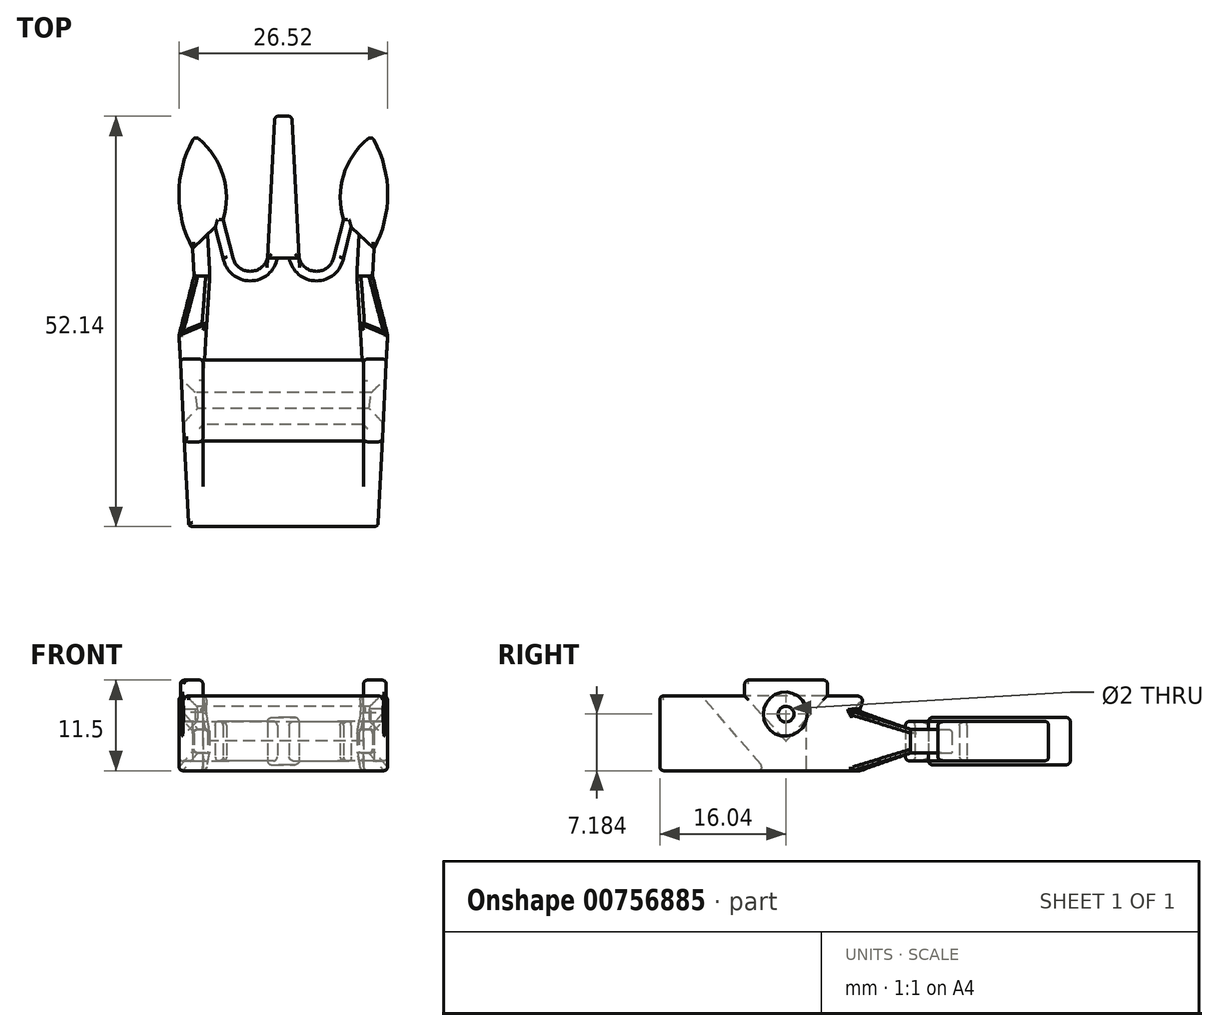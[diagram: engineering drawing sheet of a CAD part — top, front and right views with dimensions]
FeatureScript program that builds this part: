
annotation { "Feature Type Name" : "Feature", "Feature Type Description" : "" }
export const myFeature = defineFeature(function(context is Context, id is Id, definition is map)
    precondition{}
    {
        {
            var Q0;
            Q0=qCreatedBy(makeId("Top.planeOp"),FACE);
            var sketch = newSketch(context, id + "F0", { "sketchPlane" : qUnion([Q0])});
            skLineSegment(sketch, "E0", {"start": v(0, 0) * mm, "end": v(0, 18) * mm});
            skLineSegment(sketch, "E1", {"start": v(0, 0) * mm, "end": v(2, 0) * mm});
            skLineSegment(sketch, "E2", {"start": v(2, 0) * mm, "end": v(1.1, 18) * mm});
            skLineSegment(sketch, "E3", {"start": v(1.1, 18) * mm, "end": v(0, 18) * mm});
            skLineSegment(sketch, "E4", {"start": v(0, -15.6) * mm, "end": v(10.2, -15.6) * mm, "construction": true});
            skLineSegment(sketch, "E5", {"start": v(10.2, -15.6) * mm, "end": v(9.34, -2.3) * mm});
            skPoint(sketch, "E6", {"position": v(11.23, 15.5) * mm});
            skArc(sketch, "E7", {"start": v(11.53, 1.18) * mm, "mid": v(13.26, 8.38) * mm, "end": v(11.23, 15.5) * mm});
            skArc(sketch, "E8", {"start": v(11.23, 15.5) * mm, "mid": v(7.74, 10.76) * mm, "end": v(7.64, 4.86) * mm});
            skLineSegment(sketch, "E9", {"start": v(11.53, 1.18) * mm, "end": v(7.64, 4.86) * mm});
            skLineSegment(sketch, "E10", {"start": v(7.64, 4.86) * mm, "end": v(6.4, 0) * mm});
            skArc(sketch, "E11", {"start": v(2, 0) * mm, "mid": v(4.2, -1.7) * mm, "end": v(6.4, 0) * mm});
            skLineSegment(sketch, "E12", {"start": v(6.4, 0) * mm, "end": v(7.64, 0) * mm});
            skArc(sketch, "E13", {"start": v(0.76, 0) * mm, "mid": v(4.2, -2.92) * mm, "end": v(7.64, 0) * mm});
            skLineSegment(sketch, "E14", {"start": v(7.64, 0) * mm, "end": v(8.64, 3.92) * mm});
            skLineSegment(sketch, "E15", {"start": v(11.34, -2.3) * mm, "end": v(11.8, -9.27) * mm});
            skLineSegment(sketch, "E16", {"start": v(10.2, -15.6) * mm, "end": v(12.96, -15.6) * mm});
            skLineSegment(sketch, "E17", {"start": v(12.96, -15.6) * mm, "end": v(13.25, -9.87) * mm});
            skLineSegment(sketch, "E18", {"start": v(13.25, -9.87) * mm, "end": v(11.8, -9.27) * mm});
            skLineSegment(sketch, "E19", {"start": v(13.25, -9.87) * mm, "end": v(9.73, -8.42) * mm});
            skLineSegment(sketch, "E20", {"start": v(12.96, -15.6) * mm, "end": v(12.03, -34.14) * mm});
            skLineSegment(sketch, "E21", {"start": v(12.03, -34.14) * mm, "end": v(0, -34.14) * mm});
            skLineSegment(sketch, "E22", {"start": v(0, -34.14) * mm, "end": v(0, -28.82) * mm});
            skLineSegment(sketch, "E23", {"start": v(0, -28.82) * mm, "end": v(10.2, -28.82) * mm});
            skLineSegment(sketch, "E24", {"start": v(10.2, -15.6) * mm, "end": v(10.2, -28.82) * mm});
            skLineSegment(sketch, "E25", {"start": v(10.2, -20.6) * mm, "end": v(0, -20.6) * mm, "construction": true});
            skLineSegment(sketch, "E26", {"start": v(0, -20.6) * mm, "end": v(0, -15.6) * mm, "construction": true});
            skLineSegment(sketch, "E27", {"start": v(10.2, -20.6) * mm, "end": v(12.71, -20.6) * mm});
            skLineSegment(sketch, "E28", {"start": v(9.34, -2.3) * mm, "end": v(11.34, -2.3) * mm});
            skLineSegment(sketch, "E29", {"start": v(11.34, -2.3) * mm, "end": v(11.53, 1.18) * mm});
            skLineSegment(sketch, "E30", {"start": v(9.34, -2.3) * mm, "end": v(9.62, 2.99) * mm});
            skSolve(sketch);
        }
        {
            var Q0;
            {var subQ3=sQuery(id+"F0.wireOp",EDGE,"E0");Q0=makeQuery(id+"F0.imprint","IMPRINT",FACE,{"disambiguationData":[TD([[makeQuery(id+"F0.imprint","IMPRINT",EDGE,{"derivedFrom":subQ3}),-1.0]])]});}
            extrude(context, id + "F1", {"entities" : qUnion([Q0]), "depth" : 6 * mm, "offsetDistance" : 25 * mm, "symmetric" : true});
        }
        {
            var Q0;
            {var subQ0=sQuery(id+"F0.wireOp",EDGE,"E11");Q0=makeQuery(id+"F0.imprint","IMPRINT",FACE,{"disambiguationData":[TD([[makeQuery(id+"F0.imprint","IMPRINT",EDGE,{"derivedFrom":subQ0}),-1.0]])]});}
            var Q1;
            {var subQ0=sQuery(id+"F0.wireOp",EDGE,"E10");Q1=makeQuery(id+"F0.imprint","IMPRINT",FACE,{"disambiguationData":[TD([[makeQuery(id+"F0.imprint","IMPRINT",EDGE,{"derivedFrom":subQ0}),1.0]])]});}
            var Q2;
            {var subQ3=sQuery(id+"F0.wireOp",EDGE,"E7");Q2=makeQuery(id+"F0.imprint","IMPRINT",FACE,{"disambiguationData":[TD([[makeQuery(id+"F0.imprint","IMPRINT",EDGE,{"derivedFrom":subQ3}),1.0]])]});}
            extrude(context, id + "F2", {"entities" : qUnion([Q0, Q1, Q2]), "operationType" : NewBodyOperationType.ADD, "depth" : 5 * mm, "offsetDistance" : 25 * mm, "symmetric" : true});
        }
        {
            var Q0;
            {var subQ3=sQuery(id+"F0.wireOp",EDGE,"E28");Q0=makeQuery(id+"F0.imprint","IMPRINT",FACE,{"disambiguationData":[TD([[makeQuery(id+"F0.imprint","IMPRINT",EDGE,{"derivedFrom":subQ3}),1.0]])]});}
            extrude(context, id + "F3", {"entities" : qUnion([Q0]), "operationType" : NewBodyOperationType.ADD, "depth" : 3 * mm, "offsetDistance" : 25 * mm, "symmetric" : true});
        }
        {
            var Q0;
            {var subQ4=sQuery(id+"F0.wireOp",EDGE,"E16");Q0=makeQuery(id+"F0.imprint","IMPRINT",FACE,{"disambiguationData":[TD([[makeQuery(id+"F0.imprint","IMPRINT",EDGE,{"derivedFrom":subQ4}),1.0]])]});}
            var Q1;
            {var subQ0=sQuery(id+"F0.wireOp",EDGE,"E16");Q1=makeQuery(id+"F0.imprint","IMPRINT",FACE,{"disambiguationData":[TD([[makeQuery(id+"F0.imprint","IMPRINT",EDGE,{"derivedFrom":subQ0}),-1.0]])]});}
            var Q2;
            {var subQ0=sQuery(id+"F0.wireOp",EDGE,"jtnNCOtV-VjFS-6lRW-7qlV-mgHXxbnkHb78");Q2=makeQuery(id+"F0.imprint","IMPRINT",FACE,{"disambiguationData":[TD([[makeQuery(id+"F0.imprint","IMPRINT",EDGE,{"derivedFrom":subQ0}),-1.0]])]});}
            extrude(context, id + "F4", {"entities" : qUnion([Q0, Q1, Q2]), "depth" : 7.5 * mm, "offsetDistance" : 25 * mm, "symmetric" : true});
        }
        {
            var Q0;
            Q0=makeQuery(id+"F3.opExtrude","SWEPT_FACE",FACE,{"disambiguationData":[OSD([sQuery(id+"F0.wireOp",EDGE,"E28")])]});
            var Q1;
            Q1=makeQuery(id+"F4.opExtrude","SWEPT_FACE",FACE,{"disambiguationData":[OSD([sQuery(id+"F0.wireOp",EDGE,"E19")])]});
            loft(context, id + "F5", {"sheetProfilesArray" : [{ "sheetProfileEntities" : qUnion([Q0]) }, { "sheetProfileEntities" : qUnion([Q1]) }]});
        }
        {
            var Q0;
            {var subQ0=sQuery(id+"F0.wireOp",EDGE,"E21");Q0=makeQuery(id+"F0.imprint","IMPRINT",FACE,{"disambiguationData":[TD([[makeQuery(id+"F0.imprint","IMPRINT",EDGE,{"derivedFrom":subQ0}),-1.0]])]});}
            extrude(context, id + "F6", {"entities" : qUnion([Q0]), "operationType" : NewBodyOperationType.ADD, "depth" : 7.5 * mm, "offsetDistance" : 25 * mm, "symmetric" : true});
        }
        {
            var Q0;
            Q0=makeQuery(id+"F5.opLoft","SWEPT_BODY",BODY,{"disambiguationData":[OSD([sQuery(id+"F0.wireOp",EDGE,"E19"),sQuery(id+"F0.wireOp",EDGE,"E28")])]});
            var Q1;
            Q1=makeQuery(id+"F4.opExtrude","SWEPT_BODY",BODY,{"disambiguationData":[OSD([sQuery(id+"F0.wireOp",EDGE,"E5"),sQuery(id+"F0.wireOp",EDGE,"E17"),sQuery(id+"F0.wireOp",EDGE,"E19"),sQuery(id+"F0.wireOp",EDGE,"E20"),sQuery(id+"F0.wireOp",EDGE,"E24"),sQuery(id+"F0.wireOp",EDGE,"jtnNCOtV-VjFS-6lRW-7qlV-mgHXxbnkHb78"),sQuery(id+"F0.wireOp",EDGE,"VnQkR1Gs-op7I-iPq7-15UO-Wn8J0Wl9CDE5"),sQuery(id+"F0.wireOp",EDGE,"p3SSW1IA-Imiw-whqf-gpxS-0o3krwaSba9o"),sQuery(id+"F0.wireOp",EDGE,"E27")])]});
            var Q2;
            Q2=makeQuery(id+"F1.opExtrude","SWEPT_BODY",BODY,{"disambiguationData":[OSD([sQuery(id+"F0.wireOp",EDGE,"E0"),sQuery(id+"F0.wireOp",EDGE,"E1"),sQuery(id+"F0.wireOp",EDGE,"E2"),sQuery(id+"F0.wireOp",EDGE,"E3")])]});
            booleanBodies(context, id + "F7", {"operationType" : BooleanOperationType.UNION, "tools" : qUnion([Q0, Q1, Q2])});
        }
        {
            var Q0;
            {var subQ0=sQuery(id+"F0.wireOp",EDGE,"E27");var subQ1=sQuery(id+"F0.wireOp",EDGE,"E24");var subQ2=sQuery(id+"F0.wireOp",EDGE,"E20");Q0=makeQuery(id+"F6.boolean.opBoolean","MERGE",FACE,{"derivedFrom":[makeQuery(id+"F4.opExtrude","CAP_FACE",FACE,{"disambiguationData":[OSD([sQuery(id+"F0.wireOp",EDGE,"E5"),sQuery(id+"F0.wireOp",EDGE,"E17"),sQuery(id+"F0.wireOp",EDGE,"E19"),subQ2,subQ1,sQuery(id+"F0.wireOp",EDGE,"jtnNCOtV-VjFS-6lRW-7qlV-mgHXxbnkHb78"),sQuery(id+"F0.wireOp",EDGE,"VnQkR1Gs-op7I-iPq7-15UO-Wn8J0Wl9CDE5"),sQuery(id+"F0.wireOp",EDGE,"p3SSW1IA-Imiw-whqf-gpxS-0o3krwaSba9o"),subQ0])],"isStart":false}),makeQuery(id+"F6.opExtrude","CAP_FACE",FACE,{"disambiguationData":[OSD([subQ2,sQuery(id+"F0.wireOp",EDGE,"E21"),sQuery(id+"F0.wireOp",EDGE,"E22"),sQuery(id+"F0.wireOp",EDGE,"E23"),subQ1,subQ0])],"isStart":false})]});}
            extrude(context, id + "F8", {"entities" : qUnion([Q0]), "operationType" : NewBodyOperationType.ADD, "depth" : 2 * mm, "offsetDistance" : 25 * mm});
        }
        {
            var Q0;
            {var subQ0=sQuery(id+"F0.wireOp",EDGE,"E24");Q0=makeQuery(id+"F6.boolean.opBoolean","MERGE",FACE,{"derivedFrom":[makeQuery(id+"F4.opExtrude","SWEPT_FACE",FACE,{"disambiguationData":[OSD([subQ0])]}),makeQuery(id+"F6.opExtrude","SWEPT_FACE",FACE,{"disambiguationData":[OSD([subQ0])]})]});}
            var sketch = newSketch(context, id + "F9", { "sketchPlane" : qUnion([Q0])});
            skLineSegment(sketch, "E31", {"start": v(28.82, -3.75) * mm, "end": v(20.6, -3.75) * mm});
            skLineSegment(sketch, "E32", {"start": v(20.6, -3.75) * mm, "end": v(28.82, 5.75) * mm});
            skLineSegment(sketch, "E33", {"start": v(20.6, -3.75) * mm, "end": v(20.6, 0) * mm, "construction": true});
            skLineSegment(sketch, "E34", {"start": v(28.82, -3.75) * mm, "end": v(28.82, 5.75) * mm});
            skSolve(sketch);
        }
        {
            var Q0;
            Q0=makeQuery(id+"F9.imprint","IMPRINT",FACE,{"disambiguationData":[TD([[makeQuery(id+"F9.imprint","IMPRINT",EDGE,{"derivedFrom":sQuery(id+"F9.wireOp",EDGE,"E31")}),1.0]])]});
            var Q1;
            Q1=makeQuery(id+"F6.opExtrude","SWEPT_FACE",FACE,{"disambiguationData":[OSD([sQuery(id+"F0.wireOp",EDGE,"E22")])]});
            extrude(context, id + "F10", {"entities" : qUnion([Q0]), "operationType" : NewBodyOperationType.ADD, "endBound" : BoundingType.UP_TO_SURFACE, "depth" : 25 * mm, "endBoundEntityFace" : qUnion([Q1]), "offsetDistance" : 25 * mm});
        }
        {
            var Q0;
            {var subQ0=sQuery(id+"F0.wireOp",EDGE,"E24");Q0=makeQuery(id+"F6.boolean.opBoolean","MERGE",FACE,{"derivedFrom":[makeQuery(id+"F4.opExtrude","SWEPT_FACE",FACE,{"disambiguationData":[OSD([subQ0])]}),makeQuery(id+"F6.opExtrude","SWEPT_FACE",FACE,{"disambiguationData":[OSD([subQ0])]})]});}
            var sketch = newSketch(context, id + "F11", { "sketchPlane" : qUnion([Q0])});
            skLineSegment(sketch, "E35", {"start": v(18.1, 0) * mm, "end": v(12.85, 5.75) * mm});
            skLineSegment(sketch, "E36", {"start": v(18.1, 0) * mm, "end": v(23.35, 5.75) * mm});
            skLineSegment(sketch, "E37", {"start": v(23.35, 5.75) * mm, "end": v(12.85, 5.75) * mm});
            skSolve(sketch);
        }
        {
            var Q0;
            Q0 = qSketchRegion(id + "F11", true);
            extrude(context, id + "F12", {"entities" : qUnion([Q0]), "operationType" : NewBodyOperationType.REMOVE, "depth" : 25 * mm, "offsetDistance" : 25 * mm});
        }
        {
            var Q0;
            Q0=makeQuery(id+"F11.imprint","IMPRINT",FACE,{"disambiguationData":[TD([[makeQuery(id+"F11.imprint","IMPRINT",EDGE,{"derivedFrom":sQuery(id+"F11.wireOp",EDGE,"EkdtviSu-fD3E-hFDe-tVJ3-bPA0vG9ajXju")}),-1.0]])]});
            var Q1;
            {var subQ0=sQuery(id+"F11.wireOp",EDGE,"E36");Q1=makeQuery(id+"F11.imprint","IMPRINT",FACE,{"disambiguationData":[TD([[makeQuery(id+"F11.imprint","IMPRINT",EDGE,{"derivedFrom":subQ0}),1.0]])]});}
            var Q2;
            {var subQ0=sQuery(id+"F11.wireOp",EDGE,"E37");var subQ1=sQuery(id+"F11.wireOp",EDGE,"E35");var subQ2=makeQuery(id+"F11.imprint","INTERSECT",VERTEX,{"derivedFrom":[subQ1,subQ0]});Q2=makeQuery(id+"F11.imprint","IMPRINT",FACE,{"disambiguationData":[TD([[makeQuery(id+"F11.imprint","IMPRINT",EDGE,{"disambiguationData":[TD([[subQ2,1.0]])],"derivedFrom":subQ1}),-1.0]])]});}
            var Q3;
            {var subQ0=sQuery(id+"F0.wireOp",EDGE,"E22");Q3=makeQuery(id+"F10.boolean.opBoolean","MERGE",FACE,{"derivedFrom":[makeQuery(id+"F8.boolean.opBoolean","MERGE",FACE,{"derivedFrom":[makeQuery(id+"F6.opExtrude","SWEPT_FACE",FACE,{"disambiguationData":[OSD([subQ0])]}),makeQuery(id+"F8.opExtrude","SWEPT_FACE",FACE,{"disambiguationData":[OSD([subQ0])]})]}),makeQuery(id+"F10.opExtrude","CAP_FACE",FACE,{"disambiguationData":[OSD([subQ0])],"isStart":false})]});}
            extrude(context, id + "F13", {"entities" : qUnion([Q0, Q1, Q2]), "endBound" : BoundingType.UP_TO_SURFACE, "depth" : 25 * mm, "endBoundEntityFace" : qUnion([Q3]), "offsetDistance" : 25 * mm});
        }
        {
            var Q0;
            Q0=makeQuery(id+"F8.opExtrude","CAP_FACE",FACE,{"disambiguationData":[OSD([sQuery(id+"F0.wireOp",EDGE,"E5"),sQuery(id+"F0.wireOp",EDGE,"E17"),sQuery(id+"F0.wireOp",EDGE,"E19"),sQuery(id+"F0.wireOp",EDGE,"E20"),sQuery(id+"F0.wireOp",EDGE,"E21"),sQuery(id+"F0.wireOp",EDGE,"E22"),sQuery(id+"F0.wireOp",EDGE,"E23"),sQuery(id+"F0.wireOp",EDGE,"E24"),sQuery(id+"F0.wireOp",EDGE,"jtnNCOtV-VjFS-6lRW-7qlV-mgHXxbnkHb78"),sQuery(id+"F0.wireOp",EDGE,"VnQkR1Gs-op7I-iPq7-15UO-Wn8J0Wl9CDE5"),sQuery(id+"F0.wireOp",EDGE,"p3SSW1IA-Imiw-whqf-gpxS-0o3krwaSba9o"),sQuery(id+"F0.wireOp",EDGE,"E27")])],"isStart":false});
            var sketch = newSketch(context, id + "F14", { "sketchPlane" : qUnion([Q0])});
            skLineSegment(sketch, "E38", {"start": v(10.2, -12.85) * mm, "end": v(13.1, -12.85) * mm});
            skLineSegment(sketch, "E39", {"start": v(13.1, -12.85) * mm, "end": v(12.57, -23.35) * mm});
            skLineSegment(sketch, "E40", {"start": v(12.57, -23.35) * mm, "end": v(10.2, -23.35) * mm});
            skLineSegment(sketch, "E41", {"start": v(10.2, -23.35) * mm, "end": v(10.2, -12.85) * mm});
            skSolve(sketch);
        }
        {
            var Q0;
            Q0=makeQuery(id+"F14.imprint","IMPRINT",FACE,{"disambiguationData":[TD([[makeQuery(id+"F14.imprint","IMPRINT",EDGE,{"derivedFrom":sQuery(id+"F14.wireOp",EDGE,"E38")}),-1.0]])]});
            extrude(context, id + "F15", {"entities" : qUnion([Q0]), "operationType" : NewBodyOperationType.ADD, "depth" : 2 * mm, "offsetDistance" : 25 * mm});
        }
        {
            var Q0;
            {var subQ0=sQuery(id+"F11.wireOp",EDGE,"E36");Q0=makeQuery(id+"F11.imprint","IMPRINT",FACE,{"disambiguationData":[TD([[makeQuery(id+"F11.imprint","IMPRINT",EDGE,{"derivedFrom":subQ0}),1.0]])]});}
            var sketch = newSketch(context, id + "F16", { "sketchPlane" : qUnion([Q0])});
            skCircle(sketch, "E42", {"center": v(18.1, 3.43) * mm, "radius": 2.32 * mm, "construction": true});
            skCircle(sketch, "E43", {"center": v(18.1, 3.43) * mm, "radius": 1 * mm});
            skSolve(sketch);
        }
        {
            var Q0;
            Q0 = qSketchRegion(id + "F16", true);
            var Q1;
            Q1=sQuery(id+"F16.wireOp",EDGE,"E43");
            extrude(context, id + "F17", {"entities" : qUnion([Q0]), "operationType" : NewBodyOperationType.REMOVE, "surfaceEntities" : qUnion([Q1]), "endBound" : BoundingType.THROUGH_ALL, "oppositeDirection" : true, "depth" : 25 * mm, "offsetDistance" : 25 * mm, "hasSecondDirection" : true, "secondDirectionBound" : BoundingType.THROUGH_ALL, "secondDirectionOppositeDirection" : false, "secondDirectionDepth" : 25 * mm});
        }
        {
            var Q0;
            {var subQ0=sQuery(id+"F0.wireOp",EDGE,"E20");var subQ1=sQuery(id+"F0.wireOp",EDGE,"E17");Q0=makeQuery(id+"F17.boolean.opBoolean","INTERSECT",EDGE,{"derivedFrom":[makeQuery(id+"F15.boolean.opBoolean","MERGE",FACE,{"derivedFrom":[makeQuery(id+"F8.boolean.opBoolean","MERGE",FACE,{"derivedFrom":[makeQuery(id+"F6.boolean.opBoolean","MERGE",FACE,{"derivedFrom":[makeQuery(id+"F4.opExtrude","SWEPT_FACE",FACE,{"disambiguationData":[OSD([subQ1,subQ0])]}),makeQuery(id+"F6.opExtrude","SWEPT_FACE",FACE,{"disambiguationData":[OSD([subQ0])]})]}),makeQuery(id+"F8.opExtrude","SWEPT_FACE",FACE,{"disambiguationData":[OSD([subQ1,subQ0])]})]}),makeQuery(id+"F15.opExtrude","SWEPT_FACE",FACE,{"disambiguationData":[OSD([sQuery(id+"F14.wireOp",EDGE,"E39")])]})]}),makeQuery(id+"F17.opExtrude","SWEPT_FACE",FACE,{"disambiguationData":[OSD([sQuery(id+"F16.wireOp",EDGE,"E43")])]})]});}
            chamfer(context, id + "F18", {"entities" : qUnion([Q0]), "width" : 1.8 * mm});
        }
        {
            var Q0;
            Q0=makeQuery(id+"F13.opExtrude","SWEPT_EDGE",EDGE,{"disambiguationData":[OSD([sQuery(id+"F11.wireOp",EDGE,"E35"),sQuery(id+"F11.wireOp",EDGE,"E37")])]});
            var Q1;
            Q1=makeQuery(id+"F13.opExtrude","SWEPT_EDGE",EDGE,{"disambiguationData":[OSD([sQuery(id+"F0.wireOp",EDGE,"E24"),sQuery(id+"F11.wireOp",EDGE,"E36"),sQuery(id+"F11.wireOp",EDGE,"E37")])]});
            var Q2;
            Q2=makeQuery(id+"F13.opExtrude","CAP_EDGE",EDGE,{"disambiguationData":[OSD([sQuery(id+"F11.wireOp",EDGE,"E37")])],"isStart":true});
            var Q3;
            Q3=makeQuery(id+"F13.opExtrude","SWEPT_EDGE",EDGE,{"disambiguationData":[OSD([sQuery(id+"F11.wireOp",EDGE,"E35"),sQuery(id+"F11.wireOp",EDGE,"E36")])]});
            var Q4;
            Q4=makeQuery(id+"F13.opExtrude","CAP_EDGE",EDGE,{"disambiguationData":[OSD([sQuery(id+"F11.wireOp",EDGE,"E36")])],"isStart":true});
            var Q5;
            Q5=makeQuery(id+"F13.opExtrude","CAP_EDGE",EDGE,{"disambiguationData":[OSD([sQuery(id+"F11.wireOp",EDGE,"E35")])],"isStart":true});
            fillet(context, id + "F19", {"entities" : qUnion([Q0, Q1, Q2, Q3, Q4, Q5]), "radius" : .1 * mm, "tangentPropagation" : true, "allowEdgeOverflow" : false});
        }
        {
            var Q0;
            Q0=makeQuery(id+"F2.opExtrude","CAP_EDGE",EDGE,{"disambiguationData":[OSD([sQuery(id+"F0.wireOp",EDGE,"E7")])],"isStart":false});
            var Q1;
            Q1=makeQuery(id+"F2.opExtrude","CAP_EDGE",EDGE,{"disambiguationData":[OSD([sQuery(id+"F0.wireOp",EDGE,"E8")])],"isStart":false});
            var Q2;
            Q2=makeQuery(id+"F2.opExtrude","CAP_EDGE",EDGE,{"disambiguationData":[OSD([sQuery(id+"F0.wireOp",EDGE,"E7")])],"isStart":true});
            var Q3;
            Q3=makeQuery(id+"F2.opExtrude","SWEPT_EDGE",EDGE,{"disambiguationData":[OSD([sQuery(id+"F0.wireOp",EDGE,"E7"),sQuery(id+"F0.wireOp",EDGE,"E8")])]});
            var Q4;
            Q4=makeQuery(id+"F2.opExtrude","CAP_EDGE",EDGE,{"disambiguationData":[OSD([sQuery(id+"F0.wireOp",EDGE,"E8")])],"isStart":true});
            var Q5;
            Q5=makeQuery(id+"F2.opExtrude","CAP_EDGE",EDGE,{"disambiguationData":[OSD([sQuery(id+"F0.wireOp",EDGE,"E9")])],"isStart":false});
            var Q6;
            Q6=makeQuery(id+"F2.opExtrude","CAP_EDGE",EDGE,{"disambiguationData":[OSD([sQuery(id+"F0.wireOp",EDGE,"E9")])],"isStart":true});
            var Q7;
            Q7=makeQuery(id+"F1.opExtrude","CAP_EDGE",EDGE,{"disambiguationData":[OSD([sQuery(id+"F0.wireOp",EDGE,"E2")])],"isStart":false});
            var Q8;
            Q8=makeQuery(id+"F1.opExtrude","CAP_EDGE",EDGE,{"disambiguationData":[OSD([sQuery(id+"F0.wireOp",EDGE,"E1")])],"isStart":false});
            var Q9;
            Q9=makeQuery(id+"F1.opExtrude","CAP_EDGE",EDGE,{"disambiguationData":[OSD([sQuery(id+"F0.wireOp",EDGE,"E3")])],"isStart":false});
            var Q10;
            Q10=makeQuery(id+"F1.opExtrude","SWEPT_EDGE",EDGE,{"disambiguationData":[OSD([sQuery(id+"F0.wireOp",EDGE,"E2"),sQuery(id+"F0.wireOp",EDGE,"E3")])]});
            var Q11;
            Q11=makeQuery(id+"F1.opExtrude","CAP_EDGE",EDGE,{"disambiguationData":[OSD([sQuery(id+"F0.wireOp",EDGE,"E3")])],"isStart":true});
            var Q12;
            Q12=makeQuery(id+"F1.opExtrude","CAP_EDGE",EDGE,{"disambiguationData":[OSD([sQuery(id+"F0.wireOp",EDGE,"E2")])],"isStart":true});
            var Q13;
            Q13=makeQuery(id+"F1.opExtrude","CAP_EDGE",EDGE,{"disambiguationData":[OSD([sQuery(id+"F0.wireOp",EDGE,"E1")])],"isStart":true});
            var Q14;
            {var subQ0=sQuery(id+"F0.wireOp",EDGE,"E20");Q14=makeQuery(id+"F6.boolean.opBoolean","MERGE",EDGE,{"derivedFrom":[makeQuery(id+"F4.opExtrude","CAP_EDGE",EDGE,{"disambiguationData":[OSD([sQuery(id+"F0.wireOp",EDGE,"E17"),subQ0])],"isStart":true}),makeQuery(id+"F6.opExtrude","CAP_EDGE",EDGE,{"disambiguationData":[OSD([subQ0])],"isStart":true})]});}
            var Q15;
            {var subQ0=sQuery(id+"F0.wireOp",EDGE,"E19");var subQ1=sQuery(id+"F0.wireOp",EDGE,"E17");var subQ2=sQuery(id+"F0.wireOp",EDGE,"E29");var subQ3=sQuery(id+"F0.wireOp",EDGE,"E28");var subQ4=sQuery(id+"F0.wireOp",EDGE,"E15");Q15=makeQuery(id+"F5.opLoft","SWEPT_EDGE",EDGE,{"disambiguationData":[OSD([subQ4,subQ1,subQ0,subQ3,subQ2]),TDD([makeQuery(id+"F3.opExtrude","CAP_VERTEX",VERTEX,{"disambiguationData":[OSD([subQ4,subQ3,subQ2])],"isStart":true}),makeQuery(id+"F4.opExtrude","CAP_VERTEX",VERTEX,{"disambiguationData":[OSD([subQ1,subQ0])],"isStart":true})])]});}
            var Q16;
            {var subQ0=sQuery(id+"F0.wireOp",EDGE,"E19");var subQ1=sQuery(id+"F0.wireOp",EDGE,"E17");var subQ2=sQuery(id+"F0.wireOp",EDGE,"E29");var subQ3=sQuery(id+"F0.wireOp",EDGE,"E28");var subQ4=sQuery(id+"F0.wireOp",EDGE,"E15");Q16=makeQuery(id+"F5.opLoft","SWEPT_EDGE",EDGE,{"disambiguationData":[OSD([subQ4,subQ1,subQ0,subQ3,subQ2]),TDD([makeQuery(id+"F3.opExtrude","CAP_VERTEX",VERTEX,{"disambiguationData":[OSD([subQ4,subQ3,subQ2])],"isStart":false}),makeQuery(id+"F4.opExtrude","CAP_VERTEX",VERTEX,{"disambiguationData":[OSD([subQ1,subQ0])],"isStart":false})])]});}
            var Q17;
            Q17=makeQuery(id+"F3.opExtrude","CAP_EDGE",EDGE,{"disambiguationData":[OSD([sQuery(id+"F0.wireOp",EDGE,"E29")])],"isStart":true});
            var Q18;
            Q18=makeQuery(id+"F3.opExtrude","CAP_EDGE",EDGE,{"disambiguationData":[OSD([sQuery(id+"F0.wireOp",EDGE,"E29")])],"isStart":false});
            var Q19;
            Q19=makeQuery(id+"F8.opExtrude","CAP_EDGE",EDGE,{"disambiguationData":[OSD([sQuery(id+"F0.wireOp",EDGE,"E5"),sQuery(id+"F0.wireOp",EDGE,"E17"),sQuery(id+"F0.wireOp",EDGE,"E19")])],"isStart":false});
            var Q20;
            {var subQ0=sQuery(id+"F0.wireOp",EDGE,"E20");var subQ1=sQuery(id+"F0.wireOp",EDGE,"E17");Q20=makeQuery(id+"F15.boolean.opBoolean","SPLIT",EDGE,{"disambiguationData":[TD([makeQuery(id+"F15.opExtrude","SWEPT_FACE",FACE,{"disambiguationData":[OSD([sQuery(id+"F14.wireOp",EDGE,"E38")])]})])],"derivedFrom":makeQuery(id+"F8.opExtrude","CAP_EDGE",EDGE,{"disambiguationData":[OSD([subQ1,subQ0])],"isStart":false})});}
            var Q21;
            Q21=makeQuery(id+"F15.opExtrude","CAP_EDGE",EDGE,{"disambiguationData":[OSD([sQuery(id+"F14.wireOp",EDGE,"E39")])],"isStart":false});
            var Q22;
            Q22=makeQuery(id+"F15.opExtrude","CAP_EDGE",EDGE,{"disambiguationData":[OSD([sQuery(id+"F14.wireOp",EDGE,"E41")])],"isStart":false});
            var Q23;
            Q23=makeQuery(id+"F15.opExtrude","CAP_EDGE",EDGE,{"disambiguationData":[OSD([sQuery(id+"F14.wireOp",EDGE,"E38")])],"isStart":false});
            var Q24;
            {var subQ0=sQuery(id+"F0.wireOp",EDGE,"E21");var subQ1=sQuery(id+"F0.wireOp",EDGE,"E20");var subQ2=sQuery(id+"F0.wireOp",EDGE,"E17");Q24=makeQuery(id+"F15.boolean.opBoolean","SPLIT",EDGE,{"disambiguationData":[TD([makeQuery(id+"F6.opExtrude","SWEPT_FACE",FACE,{"disambiguationData":[OSD([subQ0])]})])],"derivedFrom":makeQuery(id+"F8.opExtrude","CAP_EDGE",EDGE,{"disambiguationData":[OSD([subQ2,subQ1])],"isStart":false})});}
            var Q25;
            Q25=makeQuery(id+"F12.boolean.opBoolean","MERGE",EDGE,{"derivedFrom":[makeQuery(id+"F8.opExtrude","CAP_EDGE",EDGE,{"disambiguationData":[OSD([sQuery(id+"F0.wireOp",EDGE,"E24")])],"isStart":false}),makeQuery(id+"F12.opExtrude","CAP_EDGE",EDGE,{"disambiguationData":[OSD([sQuery(id+"F11.wireOp",EDGE,"E37")])],"isStart":true})]});
            var Q26;
            Q26=makeQuery(id+"F8.opExtrude","CAP_EDGE",EDGE,{"disambiguationData":[OSD([sQuery(id+"F0.wireOp",EDGE,"E5")])],"isStart":false});
            var Q27;
            Q27=makeQuery(id+"F10.boolean.opBoolean","MERGE",EDGE,{"derivedFrom":[makeQuery(id+"F8.opExtrude","CAP_EDGE",EDGE,{"disambiguationData":[OSD([sQuery(id+"F0.wireOp",EDGE,"E23")])],"isStart":false}),makeQuery(id+"F10.opExtrude","SWEPT_EDGE",EDGE,{"disambiguationData":[OSD([sQuery(id+"F0.wireOp",EDGE,"E24"),sQuery(id+"F9.wireOp",EDGE,"E32"),sQuery(id+"F9.wireOp",EDGE,"E34")])]})]});
            var Q28;
            Q28=makeQuery(id+"F8.opExtrude","CAP_EDGE",EDGE,{"disambiguationData":[OSD([sQuery(id+"F0.wireOp",EDGE,"E21")])],"isStart":false});
            var Q29;
            {var subQ0=sQuery(id+"F0.wireOp",EDGE,"E21");var subQ1=sQuery(id+"F0.wireOp",EDGE,"E20");Q29=makeQuery(id+"F8.boolean.opBoolean","MERGE",EDGE,{"derivedFrom":[makeQuery(id+"F6.opExtrude","SWEPT_EDGE",EDGE,{"disambiguationData":[OSD([subQ1,subQ0])]}),makeQuery(id+"F8.opExtrude","SWEPT_EDGE",EDGE,{"disambiguationData":[OSD([subQ1,subQ0])]})]});}
            var Q30;
            Q30=makeQuery(id+"F6.opExtrude","CAP_EDGE",EDGE,{"disambiguationData":[OSD([sQuery(id+"F0.wireOp",EDGE,"E21")])],"isStart":true});
            var Q31;
            Q31=makeQuery(id+"F15.opExtrude","SWEPT_EDGE",EDGE,{"disambiguationData":[OSD([sQuery(id+"F0.wireOp",EDGE,"E17"),sQuery(id+"F0.wireOp",EDGE,"E20"),sQuery(id+"F14.wireOp",EDGE,"E39"),sQuery(id+"F14.wireOp",EDGE,"E40")])]});
            var Q32;
            Q32=makeQuery(id+"F15.opExtrude","SWEPT_EDGE",EDGE,{"disambiguationData":[OSD([sQuery(id+"F0.wireOp",EDGE,"E17"),sQuery(id+"F0.wireOp",EDGE,"E20"),sQuery(id+"F14.wireOp",EDGE,"E38"),sQuery(id+"F14.wireOp",EDGE,"E39")])]});
            var Q33;
            Q33=makeQuery(id+"F3.opExtrude","CAP_EDGE",EDGE,{"disambiguationData":[OSD([sQuery(id+"F0.wireOp",EDGE,"E30")])],"isStart":false});
            var Q34;
            Q34=makeQuery(id+"F10.opExtrude","SWEPT_EDGE",EDGE,{"disambiguationData":[OSD([sQuery(id+"F0.wireOp",EDGE,"E24"),sQuery(id+"F9.wireOp",EDGE,"E31"),sQuery(id+"F9.wireOp",EDGE,"E32")])]});
            var Q35;
            Q35=makeQuery(id+"F4.opExtrude","CAP_EDGE",EDGE,{"disambiguationData":[OSD([sQuery(id+"F0.wireOp",EDGE,"E5")])],"isStart":true});
            var Q36;
            {var subQ0=sQuery(id+"F0.wireOp",EDGE,"E24");Q36=makeQuery(id+"F6.boolean.opBoolean","MERGE",EDGE,{"derivedFrom":[makeQuery(id+"F4.opExtrude","CAP_EDGE",EDGE,{"disambiguationData":[OSD([subQ0])],"isStart":true}),makeQuery(id+"F6.opExtrude","CAP_EDGE",EDGE,{"disambiguationData":[OSD([subQ0])],"isStart":true})]});}
            var Q37;
            {var subQ0=sQuery(id+"F0.wireOp",EDGE,"E19");var subQ1=sQuery(id+"F0.wireOp",EDGE,"E5");var subQ2=sQuery(id+"F0.wireOp",EDGE,"E30");var subQ3=sQuery(id+"F0.wireOp",EDGE,"E28");Q37=makeQuery(id+"F5.opLoft","SWEPT_EDGE",EDGE,{"disambiguationData":[OSD([subQ1,subQ0,subQ3,subQ2]),TDD([makeQuery(id+"F3.opExtrude","CAP_VERTEX",VERTEX,{"disambiguationData":[OSD([subQ1,subQ3,subQ2])],"isStart":true}),makeQuery(id+"F4.opExtrude","CAP_VERTEX",VERTEX,{"disambiguationData":[OSD([subQ1,subQ0])],"isStart":true})])]});}
            var Q38;
            {var subQ0=sQuery(id+"F0.wireOp",EDGE,"E0");var subQ1=makeQuery(id+"F20.opFillet","BLEND_EDGE",EDGE,{"blendedFrom":[makeQuery(id+"F1.opExtrude","CAP_EDGE",EDGE,{"disambiguationData":[OSD([subQ0])],"isStart":false}),makeQuery(id+"F1.opExtrude","SWEPT_FACE",FACE,{"disambiguationData":[OSD([subQ0])]})],"blendedInto":[makeQuery(id+"F1.opExtrude","SWEPT_FACE",FACE,{"disambiguationData":[OSD([subQ0])]})]});Q38=makeQuery(id+"F24.opBoolean","MERGE",EDGE,{"derivedFrom":[subQ1,makeQuery(id+"F23.opPattern","COPY",EDGE,{"derivedFrom":subQ1,"instanceName":"1"})]});}
            fillet(context, id + "F20", {"entities" : qUnion([Q0, Q1, Q2, Q3, Q4, Q5, Q6, Q7, Q8, Q9, Q10, Q11, Q12, Q13, Q14, Q15, Q16, Q17, Q18, Q19, Q20, Q21, Q22, Q23, Q24, Q25, Q26, Q27, Q28, Q29, Q30, Q31, Q32, Q33, Q34, Q35, Q36, Q37, Q38]), "radius" : 0.5 * mm, "allowEdgeOverflow" : false});
        }
        {
            var Q0;
            Q0=makeQuery(id+"F2.opExtrude","CAP_EDGE",EDGE,{"disambiguationData":[OSD([sQuery(id+"F0.wireOp",EDGE,"E10")])],"isStart":true});
            var Q1;
            Q1=makeQuery(id+"F2.opExtrude","CAP_EDGE",EDGE,{"disambiguationData":[OSD([sQuery(id+"F0.wireOp",EDGE,"E14")])],"isStart":true});
            var Q2;
            Q2=makeQuery(id+"F2.opExtrude","CAP_EDGE",EDGE,{"disambiguationData":[OSD([sQuery(id+"F0.wireOp",EDGE,"E13")])],"isStart":true});
            var Q3;
            Q3=makeQuery(id+"F2.opExtrude","CAP_EDGE",EDGE,{"disambiguationData":[OSD([sQuery(id+"F0.wireOp",EDGE,"E10")])],"isStart":false});
            var Q4;
            Q4=makeQuery(id+"F2.opExtrude","CAP_EDGE",EDGE,{"disambiguationData":[OSD([sQuery(id+"F0.wireOp",EDGE,"E14")])],"isStart":false});
            var Q5;
            Q5=makeQuery(id+"F2.opExtrude","CAP_EDGE",EDGE,{"disambiguationData":[OSD([sQuery(id+"F0.wireOp",EDGE,"E13")])],"isStart":false});
            fillet(context, id + "F21", {"entities" : qUnion([Q0, Q1, Q2, Q3, Q4, Q5]), "radius" : .5 * mm, "tangentPropagation" : true, "allowEdgeOverflow" : false});
        }
        {
            var Q0;
            {var subQ0=sQuery(id+"F0.wireOp",EDGE,"E19");var subQ1=sQuery(id+"F0.wireOp",EDGE,"E5");var subQ2=sQuery(id+"F0.wireOp",EDGE,"E30");var subQ3=sQuery(id+"F0.wireOp",EDGE,"E28");Q0=makeQuery(id+"F5.opLoft","SWEPT_EDGE",EDGE,{"disambiguationData":[OSD([subQ1,subQ0,subQ3,subQ2]),TDD([makeQuery(id+"F3.opExtrude","CAP_VERTEX",VERTEX,{"disambiguationData":[OSD([subQ1,subQ3,subQ2])],"isStart":false}),makeQuery(id+"F4.opExtrude","CAP_VERTEX",VERTEX,{"disambiguationData":[OSD([subQ1,subQ0])],"isStart":false})])]});}
            var Q1;
            Q1=makeQuery(id+"F10.opExtrude","CAP_EDGE",EDGE,{"disambiguationData":[OSD([sQuery(id+"F9.wireOp",EDGE,"E32")])],"isStart":true});
            var Q2;
            Q2=makeQuery(id+"F15.opExtrude","SWEPT_EDGE",EDGE,{"disambiguationData":[OSD([sQuery(id+"F0.wireOp",EDGE,"E24"),sQuery(id+"F11.wireOp",EDGE,"E37"),sQuery(id+"F14.wireOp",EDGE,"E40"),sQuery(id+"F14.wireOp",EDGE,"E41")])]});
            var Q3;
            Q3=makeQuery(id+"F15.opExtrude","SWEPT_EDGE",EDGE,{"disambiguationData":[OSD([sQuery(id+"F11.wireOp",EDGE,"E35"),sQuery(id+"F11.wireOp",EDGE,"E37"),sQuery(id+"F14.wireOp",EDGE,"E38"),sQuery(id+"F14.wireOp",EDGE,"E41")])]});
            var Q4;
            {var subQ0=sQuery(id+"F0.wireOp",EDGE,"E19");var subQ1=sQuery(id+"F0.wireOp",EDGE,"E17");var subQ2=sQuery(id+"F0.wireOp",EDGE,"E5");var subQ3=makeQuery(id+"F4.opExtrude","CAP_EDGE",EDGE,{"disambiguationData":[OSD([subQ0])],"isStart":false});Q4=makeQuery(id+"F8.boolean.opBoolean","MERGE",EDGE,{"derivedFrom":[makeQuery(id+"F7.opBoolean","MERGE",EDGE,{"derivedFrom":[subQ3,makeQuery(id+"F5.opLoft","MID_CAP_EDGE",EDGE,{"disambiguationData":[OSD([subQ2,subQ1,subQ0]),TDD([makeQuery(id+"F4.opExtrude","CAP_VERTEX",VERTEX,{"disambiguationData":[OSD([subQ1,subQ0])],"isStart":false}),makeQuery(id+"F4.opExtrude","CAP_VERTEX",VERTEX,{"disambiguationData":[OSD([subQ2,subQ0])],"isStart":false}),subQ3])],"capPos":1.0})]}),makeQuery(id+"F8.opExtrude","CAP_EDGE",EDGE,{"disambiguationData":[OSD([subQ2,subQ1,subQ0])],"isStart":true})]});}
            var Q5;
            {var subQ0=sQuery(id+"F0.wireOp",EDGE,"E19");var subQ1=sQuery(id+"F0.wireOp",EDGE,"E17");Q5=makeQuery(id+"F7.opBoolean","MERGE",EDGE,{"derivedFrom":[makeQuery(id+"F4.opExtrude","SWEPT_EDGE",EDGE,{"disambiguationData":[OSD([subQ1,subQ0])]}),makeQuery(id+"F5.opLoft","MID_CAP_EDGE",EDGE,{"disambiguationData":[OSD([subQ1,subQ0])],"capPos":1.0})]});}
            fillet(context, id + "F22", {"entities" : qUnion([Q0, Q1, Q2, Q3, Q4, Q5]), "radius" : .5 * mm, "tangentPropagation" : true, "allowEdgeOverflow" : false});
        }
        {
            var Q0;
            Q0=makeQuery(id+"F13.opExtrude","SWEPT_BODY",BODY,{"disambiguationData":[OSD([sQuery(id+"F11.wireOp",EDGE,"E35"),sQuery(id+"F11.wireOp",EDGE,"E36"),sQuery(id+"F11.wireOp",EDGE,"E37")])]});
            var Q1;
            Q1=makeQuery(id+"F5.opLoft","SWEPT_BODY",BODY,{"disambiguationData":[OSD([sQuery(id+"F0.wireOp",EDGE,"E19"),sQuery(id+"F0.wireOp",EDGE,"E28")])]});
            var Q2;
            Q2=qCreatedBy(makeId("Right.planeOp"),FACE);
            mirror(context, id + "F23", {"entities" : qUnion([Q0, Q1]), "mirrorPlane" : qUnion([Q2])});
        }
        {
            var Q0;
            Q0=makeQuery(id+"F5.opLoft","SWEPT_BODY",BODY,{"disambiguationData":[OSD([sQuery(id+"F0.wireOp",EDGE,"E19"),sQuery(id+"F0.wireOp",EDGE,"E28")])]});
            var Q1;
            Q1=makeQuery(id+"F23.opPattern","COPY",BODY,{"derivedFrom":makeQuery(id+"F5.opLoft","SWEPT_BODY",BODY,{"disambiguationData":[OSD([sQuery(id+"F0.wireOp",EDGE,"E19"),sQuery(id+"F0.wireOp",EDGE,"E28")])]}),"instanceName":"1"});
            booleanBodies(context, id + "F24", {"operationType" : BooleanOperationType.UNION, "tools" : qUnion([Q0, Q1])});
        }
    });
